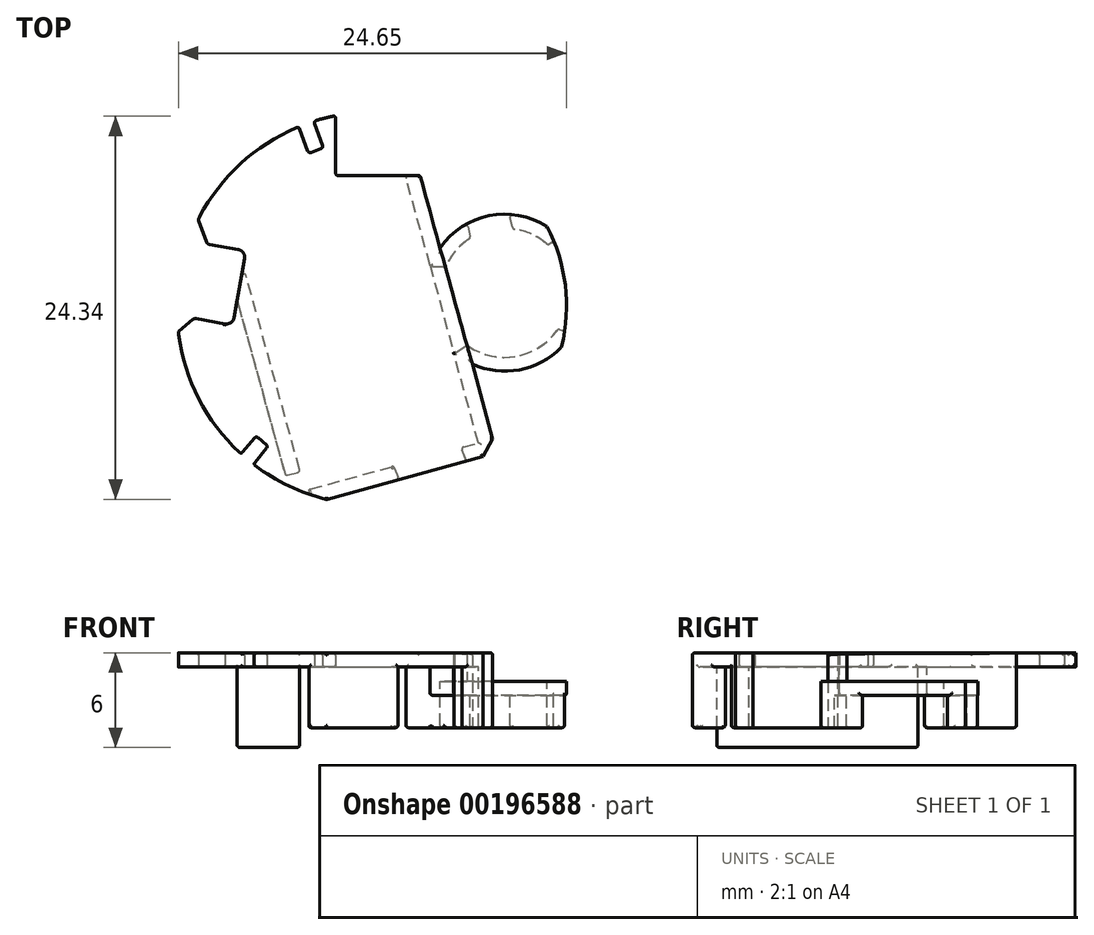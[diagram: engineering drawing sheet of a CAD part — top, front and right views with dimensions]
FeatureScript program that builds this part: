
annotation { "Feature Type Name" : "Feature", "Feature Type Description" : "" }
export const myFeature = defineFeature(function(context is Context, id is Id, definition is map)
    precondition{}
    {
        {
            var Q0;
            Q0=qCreatedBy(makeId("Top.planeOp"),FACE);
            var sketch = newSketch(context, id + "F0", { "sketchPlane" : qUnion([Q0])});
            skArc(sketch, "E0.0", {"start": v(-8.3, -9.34) * mm, "mid": v(-12.3, 2.17) * mm, "end": v(-4.6, 11.61) * mm});
            skLineSegment(sketch, "E0.1", {"start": v(-4.03, 10.06) * mm, "end": v(-4.6, 11.61) * mm});
            skLineSegment(sketch, "E0.2", {"start": v(-3.38, 10.3) * mm, "end": v(-4.03, 10.06) * mm});
            skLineSegment(sketch, "E0.3", {"start": v(-3.94, 11.85) * mm, "end": v(-3.38, 10.3) * mm});
            skArc(sketch, "E0.4", {"start": v(11.5, 4.86) * mm, "mid": v(5.15, 11.38) * mm, "end": v(-3.94, 11.85) * mm});
            skArc(sketch, "E0.5", {"start": v(9.59, 5.84) * mm, "mid": v(10.6, 5.46) * mm, "end": v(11.5, 4.86) * mm});
            skLineSegment(sketch, "E0.6", {"start": v(9.3, 7.1) * mm, "end": v(9.59, 5.84) * mm});
            skLineSegment(sketch, "E0.7", {"start": v(8.43, 6.91) * mm, "end": v(9.3, 7.1) * mm});
            skLineSegment(sketch, "E0.8", {"start": v(8.84, 5.07) * mm, "end": v(8.43, 6.91) * mm});
            skArc(sketch, "E0.9", {"start": v(11.07, 4.05) * mm, "mid": v(10.03, 4.73) * mm, "end": v(8.84, 5.07) * mm});
            skLineSegment(sketch, "E0.10", {"start": v(11.7, 4.37) * mm, "end": v(11.07, 4.05) * mm});
            skArc(sketch, "E0.11", {"start": v(12.4, -1.48) * mm, "mid": v(12.4, 1.49) * mm, "end": v(11.7, 4.37) * mm});
            skLineSegment(sketch, "E0.12", {"start": v(11.72, -1.31) * mm, "end": v(12.4, -1.48) * mm});
            skArc(sketch, "E0.13", {"start": v(5.93, -2.32) * mm, "mid": v(9.03, -3.04) * mm, "end": v(11.72, -1.31) * mm});
            skLineSegment(sketch, "E0.14", {"start": v(5.1, -2.88) * mm, "end": v(5.93, -2.32) * mm});
            skLineSegment(sketch, "E0.15", {"start": v(6.66, -8.53) * mm, "end": v(5.1, -2.88) * mm});
            skArc(sketch, "E0.16", {"start": v(12.33, -2) * mm, "mid": v(9.57, -3.82) * mm, "end": v(6.29, -3.53) * mm});
            skLineSegment(sketch, "E0.17", {"start": v(6.29, -3.53) * mm, "end": v(7.57, -8.28) * mm});
            skArc(sketch, "E0.18", {"start": v(12.33, -2) * mm, "mid": v(6.89, -10.42) * mm, "end": v(-2.99, -12.13) * mm});
            skArc(sketch, "E0.19", {"start": v(4.56, 2.62) * mm, "mid": v(5.22, 3.67) * mm, "end": v(6.15, 4.47) * mm});
            skLineSegment(sketch, "E0.20", {"start": v(4.56, 2.62) * mm, "end": v(3.62, 2.67) * mm});
            skLineSegment(sketch, "E0.21", {"start": v(3.62, 2.67) * mm, "end": v(1.3, 11.05) * mm});
            skLineSegment(sketch, "E0.22", {"start": v(5.74, 6.32) * mm, "end": v(6.15, 4.47) * mm});
            skLineSegment(sketch, "E0.23", {"start": v(4.86, 6.12) * mm, "end": v(5.74, 6.32) * mm});
            skLineSegment(sketch, "E0.24", {"start": v(5.14, 4.85) * mm, "end": v(4.86, 6.12) * mm});
            skArc(sketch, "E0.25", {"start": v(4.22, 3.85) * mm, "mid": v(4.65, 4.38) * mm, "end": v(5.14, 4.85) * mm});
            skLineSegment(sketch, "E0.26", {"start": v(2.17, 11.3) * mm, "end": v(4.22, 3.85) * mm});
            skLineSegment(sketch, "E0.27", {"start": v(1.3, 11.05) * mm, "end": v(2.17, 11.3) * mm});
            skLineSegment(sketch, "E0.28", {"start": v(5.57, -8.83) * mm, "end": v(6.66, -8.53) * mm});
            skLineSegment(sketch, "E0.29", {"start": v(5.88, -9.68) * mm, "end": v(5.57, -8.83) * mm});
            skLineSegment(sketch, "E0.30", {"start": v(7.57, -8.28) * mm, "end": v(6.94, -9.38) * mm});
            skLineSegment(sketch, "E0.31", {"start": v(6.94, -9.38) * mm, "end": v(5.88, -9.68) * mm});
            skLineSegment(sketch, "E0.32", {"start": v(1.6, -10.86) * mm, "end": v(-2.99, -12.13) * mm});
            skLineSegment(sketch, "E0.33", {"start": v(1.29, -10.01) * mm, "end": v(1.6, -10.86) * mm});
            skLineSegment(sketch, "E0.34", {"start": v(-4.14, -11.51) * mm, "end": v(1.29, -10.01) * mm});
            skLineSegment(sketch, "E0.35", {"start": v(-4.06, -11.81) * mm, "end": v(-4.14, -11.51) * mm});
            skArc(sketch, "E0.36", {"start": v(-4.06, -11.81) * mm, "mid": v(-6, -10.96) * mm, "end": v(-7.76, -9.79) * mm});
            skLineSegment(sketch, "E0.37", {"start": v(-8.3, -9.34) * mm, "end": v(-7.44, -8.32) * mm});
            skLineSegment(sketch, "E0.38", {"start": v(-7.44, -8.32) * mm, "end": v(-6.9, -8.77) * mm});
            skLineSegment(sketch, "E0.39", {"start": v(-6.9, -8.77) * mm, "end": v(-7.76, -9.79) * mm});
            skLineSegment(sketch, "E1", {"start": v(-9.35, -0.48) * mm, "end": v(-8.69, 3.26) * mm});
            skLineSegment(sketch, "E2", {"start": v(-8.69, 3.26) * mm, "end": v(-10.66, 3.61) * mm});
            skLineSegment(sketch, "E3", {"start": v(-10.66, 3.61) * mm, "end": v(-11.32, -0.13) * mm});
            skLineSegment(sketch, "E4", {"start": v(-11.32, -0.13) * mm, "end": v(-9.35, -0.48) * mm});
            skLineSegment(sketch, "E5", {"start": v(0, 0) * mm, "end": v(-7.77, 0) * mm, "construction": true});
            skLineSegment(sketch, "E6", {"start": v(3.92, 8.2) * mm, "end": v(7.03, 6.03) * mm});
            skLineSegment(sketch, "E7", {"start": v(7.03, 6.03) * mm, "end": v(8.18, 7.67) * mm});
            skLineSegment(sketch, "E8", {"start": v(8.18, 7.67) * mm, "end": v(5.06, 9.85) * mm});
            skLineSegment(sketch, "E9", {"start": v(5.06, 9.85) * mm, "end": v(3.92, 8.2) * mm});
            skLineSegment(sketch, "E10", {"start": v(0, 0) * mm, "end": v(10.4, 0) * mm, "construction": true});
            skLineSegment(sketch, "E11.0", {"start": v(-11.28, -0.65) * mm, "end": v(-9.43, -0.97) * mm});
            skLineSegment(sketch, "E12.0", {"start": v(-8.86, -0.57) * mm, "end": v(-8.2, 3.18) * mm});
            skLineSegment(sketch, "E13.0", {"start": v(-8.6, 3.76) * mm, "end": v(-10.43, 4.08) * mm});
            skLineSegment(sketch, "E14", {"start": v(-10.62, 4.24) * mm, "end": v(-11.14, 5.66) * mm});
            skLineSegment(sketch, "E15", {"start": v(-11.49, -0.7) * mm, "end": v(-12.4, -1.47) * mm});
            skArc(sketch, "E16", {"start": v(-8.2, 3.18) * mm, "mid": v(-8.28, 3.55) * mm, "end": v(-8.6, 3.76) * mm});
            skArc(sketch, "E17", {"start": v(-9.43, -0.97) * mm, "mid": v(-9.06, -0.89) * mm, "end": v(-8.86, -0.57) * mm});
            skLineSegment(sketch, "E18", {"start": v(2.17, 11.3) * mm, "end": v(1.88, 12.35) * mm});
            skLineSegment(sketch, "E19", {"start": v(7.57, -8.28) * mm, "end": v(7.95, -9.64) * mm});
            skLineSegment(sketch, "E20", {"start": v(4.56, 2.62) * mm, "end": v(5.93, -2.32) * mm});
            skLineSegment(sketch, "E21.0", {"start": v(-4.18, 10) * mm, "end": v(-4.74, 11.56) * mm});
            skLineSegment(sketch, "E22.0", {"start": v(-3.8, 11.9) * mm, "end": v(-3.24, 10.35) * mm});
            skLineSegment(sketch, "E23.0", {"start": v(-3.33, 10.16) * mm, "end": v(-3.98, 9.92) * mm});
            skArc(sketch, "E24", {"start": v(-4.18, 10) * mm, "mid": v(-4.1, 9.92) * mm, "end": v(-3.98, 9.92) * mm});
            skArc(sketch, "E25", {"start": v(-3.33, 10.16) * mm, "mid": v(-3.24, 10.24) * mm, "end": v(-3.24, 10.35) * mm});
            skLineSegment(sketch, "E26.0", {"start": v(-8.4, -9.24) * mm, "end": v(-7.55, -8.22) * mm});
            skLineSegment(sketch, "E27.0", {"start": v(-6.79, -8.86) * mm, "end": v(-7.64, -9.89) * mm});
            skLineSegment(sketch, "E28.0", {"start": v(-7.34, -8.2) * mm, "end": v(-6.8, -8.65) * mm});
            skArc(sketch, "E29", {"start": v(-6.79, -8.86) * mm, "mid": v(-6.75, -8.75) * mm, "end": v(-6.8, -8.65) * mm});
            skArc(sketch, "E30", {"start": v(-7.34, -8.2) * mm, "mid": v(-7.45, -8.17) * mm, "end": v(-7.55, -8.22) * mm});
            skLineSegment(sketch, "E31", {"start": v(6.29, -3.53) * mm, "end": v(5.93, -2.32) * mm});
            skCircle(sketch, "E32", {"center": v(0, 0) * mm, "radius": 12.49 * mm});
            skLineSegment(sketch, "E33", {"start": v(4.22, 3.85) * mm, "end": v(4.56, 2.62) * mm});
            skLineSegment(sketch, "E34", {"start": v(-4.66, -10.36) * mm, "end": v(-8.27, 2.73) * mm});
            skLineSegment(sketch, "E35", {"start": v(-8.66, 0.52) * mm, "end": v(-5.6, -10.61) * mm});
            skLineSegment(sketch, "E36", {"start": v(-5.6, -10.61) * mm, "end": v(-4.66, -10.36) * mm});
            skLineSegment(sketch, "E37", {"start": v(1.6, -10.86) * mm, "end": v(2, -12.33) * mm});
            skLineSegment(sketch, "E38", {"start": v(5.88, -9.68) * mm, "end": v(6.2, -10.84) * mm});
            skLineSegment(sketch, "E39", {"start": v(6.2, -10.84) * mm, "end": v(5.88, -9.68) * mm});
            skLineSegment(sketch, "E40", {"start": v(5.88, -9.68) * mm, "end": v(1.6, -10.86) * mm});
            skPoint(sketch, "E41.visualSharp", {"position": v(-10.57, 4.1) * mm});
            skArc(sketch, "E41.filletArc", {"start": v(-10.62, 4.24) * mm, "mid": v(-10.55, 4.13) * mm, "end": v(-10.43, 4.08) * mm});
            skPoint(sketch, "E42.visualSharp", {"position": v(-11.4, -0.63) * mm});
            skArc(sketch, "E42.filletArc", {"start": v(-11.28, -0.65) * mm, "mid": v(-11.4, -0.65) * mm, "end": v(-11.49, -0.7) * mm});
            skLineSegment(sketch, "E43.bottom", {"start": v(-2.4, 13.27) * mm, "end": v(2.4, 13.27) * mm});
            skLineSegment(sketch, "E43.top", {"start": v(-2.4, 8.45) * mm, "end": v(2.4, 8.45) * mm});
            skLineSegment(sketch, "E43.left", {"start": v(-2.4, 13.27) * mm, "end": v(-2.4, 8.45) * mm});
            skLineSegment(sketch, "E43.right", {"start": v(2.4, 13.27) * mm, "end": v(2.4, 8.45) * mm});
            skLineSegment(sketch, "E44", {"start": v(2.4, 8.45) * mm, "end": v(2.95, 8.45) * mm});
            skCircle(sketch, "E45", {"center": v(8.33, 1) * mm, "radius": 4.1 * mm});
            skCircle(sketch, "E46", {"center": v(8.33, 1) * mm, "radius": 5 * mm});
            skArc(sketch, "E47", {"start": v(11.94, -2.46) * mm, "mid": v(12.18, 1.46) * mm, "end": v(11.02, 5.22) * mm});
            skLineSegment(sketch, "E48", {"start": v(3.62, 2.67) * mm, "end": v(5.1, -2.88) * mm});
            skSolve(sketch);
        }
        {
            var Q0;
            {var subQ30=sQuery(id+"F0.wireOp",EDGE,"E0.28");Q0=makeQuery(id+"F0.imprint","IMPRINT",FACE,{"disambiguationData":[TD([[makeQuery(id+"F0.imprint","IMPRINT",EDGE,{"derivedFrom":subQ30}),1.0]])]});}
            var Q1;
            {var subQ0=sQuery(id+"F0.wireOp",EDGE,"E34");Q1=makeQuery(id+"F0.imprint","IMPRINT",FACE,{"disambiguationData":[TD([[makeQuery(id+"F0.imprint","IMPRINT",EDGE,{"derivedFrom":subQ0}),1.0]])]});}
            var Q2;
            {var subQ1=sQuery(id+"F0.wireOp",EDGE,"E0.32");Q2=makeQuery(id+"F0.imprint","IMPRINT",FACE,{"disambiguationData":[TD([[makeQuery(id+"F0.imprint","IMPRINT",EDGE,{"derivedFrom":subQ1}),-1.0]])]});}
            var Q3;
            {var subQ0=sQuery(id+"F0.wireOp",EDGE,"E44");Q3=makeQuery(id+"F0.imprint","IMPRINT",FACE,{"disambiguationData":[TD([[makeQuery(id+"F0.imprint","IMPRINT",EDGE,{"derivedFrom":subQ0}),-1.0]])]});}
            var Q4;
            {var subQ6=sQuery(id+"F0.wireOp",EDGE,"E0.20");Q4=makeQuery(id+"F0.imprint","IMPRINT",FACE,{"disambiguationData":[TD([[makeQuery(id+"F0.imprint","IMPRINT",EDGE,{"derivedFrom":subQ6}),1.0]])]});}
            var Q5;
            {var subQ0=sQuery(id+"F0.wireOp",EDGE,"E31");Q5=makeQuery(id+"F0.imprint","IMPRINT",FACE,{"disambiguationData":[TD([[makeQuery(id+"F0.imprint","IMPRINT",EDGE,{"derivedFrom":subQ0}),1.0]])]});}
            var Q6;
            {var subQ4=sQuery(id+"F0.wireOp",EDGE,"E0.15");Q6=makeQuery(id+"F0.imprint","IMPRINT",FACE,{"disambiguationData":[TD([[makeQuery(id+"F0.imprint","IMPRINT",EDGE,{"derivedFrom":subQ4}),-1.0]])]});}
            var Q7;
            {var subQ0=sQuery(id+"F0.wireOp",EDGE,"E0.20");Q7=makeQuery(id+"F0.imprint","IMPRINT",FACE,{"disambiguationData":[TD([[makeQuery(id+"F0.imprint","IMPRINT",EDGE,{"derivedFrom":subQ0}),-1.0]])]});}
            var Q8;
            {var subQ0=sQuery(id+"F0.wireOp",EDGE,"E20");Q8=makeQuery(id+"F0.imprint","IMPRINT",FACE,{"disambiguationData":[TD([[makeQuery(id+"F0.imprint","IMPRINT",EDGE,{"derivedFrom":subQ0}),-1.0]])]});}
            var Q9;
            {var subQ0=sQuery(id+"F0.wireOp",EDGE,"E48");var subQ1=sQuery(id+"F0.wireOp",EDGE,"E46");var subQ3=makeQuery(id+"F0.imprint","INTERSECT",VERTEX,{"derivedFrom":[subQ1,subQ0]});Q9=makeQuery(id+"F0.imprint","IMPRINT",FACE,{"disambiguationData":[TD([[makeQuery(id+"F0.imprint","IMPRINT",EDGE,{"disambiguationData":[TD([[subQ3,1.0]])],"derivedFrom":subQ1}),1.0]])]});}
            extrude(context, id + "F1", {"entities" : qUnion([Q0, Q1, Q2, Q3, Q4, Q5, Q6, Q7, Q8, Q9]), "depth" : .9 * mm});
        }
        {
            var Q0;
            {var subQ1=sQuery(id+"F0.wireOp",EDGE,"E0.32");Q0=makeQuery(id+"F0.imprint","IMPRINT",FACE,{"disambiguationData":[TD([[makeQuery(id+"F0.imprint","IMPRINT",EDGE,{"derivedFrom":subQ1}),-1.0]])]});}
            var Q1;
            {var subQ9=sQuery(id+"F0.wireOp",EDGE,"E0.17");Q1=makeQuery(id+"F0.imprint","IMPRINT",FACE,{"disambiguationData":[TD([[makeQuery(id+"F0.imprint","IMPRINT",EDGE,{"derivedFrom":subQ9}),-1.0]])]});}
            var Q2;
            {var subQ3=sQuery(id+"F0.wireOp",EDGE,"E44");Q2=makeQuery(id+"F0.imprint","IMPRINT",FACE,{"disambiguationData":[TD([[makeQuery(id+"F0.imprint","IMPRINT",EDGE,{"derivedFrom":subQ3}),-1.0]])]});}
            var Q3;
            {var subQ0=sQuery(id+"F0.wireOp",EDGE,"E0.20");Q3=makeQuery(id+"F0.imprint","IMPRINT",FACE,{"disambiguationData":[TD([[makeQuery(id+"F0.imprint","IMPRINT",EDGE,{"derivedFrom":subQ0}),-1.0]])]});}
            var Q4;
            {var subQ4=sQuery(id+"F0.wireOp",EDGE,"E0.15");Q4=makeQuery(id+"F0.imprint","IMPRINT",FACE,{"disambiguationData":[TD([[makeQuery(id+"F0.imprint","IMPRINT",EDGE,{"derivedFrom":subQ4}),-1.0]])]});}
            extrude(context, id + "F2", {"entities" : qUnion([Q0, Q1, Q2, Q3, Q4]), "operationType" : NewBodyOperationType.ADD, "oppositeDirection" : true, "depth" : (5.2 - .1 - 1.25) * mm});
        }
        {
            var Q0;
            {var subQ0=sQuery(id+"F0.wireOp",EDGE,"E34");Q0=makeQuery(id+"F0.imprint","IMPRINT",FACE,{"disambiguationData":[TD([[makeQuery(id+"F0.imprint","IMPRINT",EDGE,{"derivedFrom":subQ0}),1.0]])]});}
            extrude(context, id + "F3", {"entities" : qUnion([Q0]), "operationType" : NewBodyOperationType.ADD, "oppositeDirection" : true, "depth" : (5.2 - .1) * mm});
        }
        {
            var Q0;
            {var subQ3=sQuery(id+"F0.wireOp",EDGE,"E31");Q0=makeQuery(id+"F0.imprint","IMPRINT",FACE,{"disambiguationData":[TD([[makeQuery(id+"F0.imprint","IMPRINT",EDGE,{"derivedFrom":subQ3}),-1.0]])]});}
            var Q1;
            {var subQ3=sQuery(id+"F0.wireOp",EDGE,"E20");Q1=makeQuery(id+"F0.imprint","IMPRINT",FACE,{"disambiguationData":[TD([[makeQuery(id+"F0.imprint","IMPRINT",EDGE,{"derivedFrom":subQ3}),1.0]])]});}
            var Q2;
            {var subQ5=sQuery(id+"F0.wireOp",EDGE,"E33");Q2=makeQuery(id+"F0.imprint","IMPRINT",FACE,{"disambiguationData":[TD([[makeQuery(id+"F0.imprint","IMPRINT",EDGE,{"derivedFrom":subQ5}),1.0]])]});}
            var Q3;
            {var subQ0=sQuery(id+"F0.wireOp",EDGE,"E45");var subQ1=sQuery(id+"F0.wireOp",EDGE,"E0.8");var subQ2=makeQuery(id+"F0.imprint","INTERSECT",VERTEX,{"derivedFrom":[subQ1,subQ0]});Q3=makeQuery(id+"F0.imprint","IMPRINT",FACE,{"disambiguationData":[TD([[makeQuery(id+"F0.imprint","IMPRINT",EDGE,{"disambiguationData":[TD([[subQ2,-1.0]])],"derivedFrom":subQ1}),1.0]])]});}
            var Q4;
            {var subQ4=sQuery(id+"F0.wireOp",EDGE,"E45");var subQ5=sQuery(id+"F0.wireOp",EDGE,"E0.8");var subQ6=makeQuery(id+"F0.imprint","INTERSECT",VERTEX,{"derivedFrom":[subQ5,subQ4]});Q4=makeQuery(id+"F0.imprint","IMPRINT",FACE,{"disambiguationData":[TD([[makeQuery(id+"F0.imprint","IMPRINT",EDGE,{"disambiguationData":[TD([[subQ6,-1.0]])],"derivedFrom":subQ5}),-1.0]])]});}
            var Q5;
            {var subQ0=sQuery(id+"F0.wireOp",EDGE,"E45");var subQ1=sQuery(id+"F0.wireOp",EDGE,"E0.10");var subQ2=makeQuery(id+"F0.imprint","INTERSECT",VERTEX,{"derivedFrom":[subQ1,subQ0]});Q5=makeQuery(id+"F0.imprint","IMPRINT",FACE,{"disambiguationData":[TD([[makeQuery(id+"F0.imprint","IMPRINT",EDGE,{"disambiguationData":[TD([[subQ2,1.0]])],"derivedFrom":subQ1}),1.0]])]});}
            var Q6;
            {var subQ0=sQuery(id+"F0.wireOp",EDGE,"E45");var subQ1=sQuery(id+"F0.wireOp",EDGE,"E0.12");var subQ2=makeQuery(id+"F0.imprint","INTERSECT",VERTEX,{"derivedFrom":[subQ1,subQ0]});Q6=makeQuery(id+"F0.imprint","IMPRINT",FACE,{"disambiguationData":[TD([[makeQuery(id+"F0.imprint","IMPRINT",EDGE,{"disambiguationData":[TD([[subQ2,-1.0]])],"derivedFrom":subQ1}),1.0]])]});}
            var Q7;
            {var subQ0=sQuery(id+"F0.wireOp",EDGE,"E20");Q7=makeQuery(id+"F0.imprint","IMPRINT",FACE,{"disambiguationData":[TD([[makeQuery(id+"F0.imprint","IMPRINT",EDGE,{"derivedFrom":subQ0}),-1.0]])]});}
            var Q8;
            {var subQ0=sQuery(id+"F0.wireOp",EDGE,"E0.20");Q8=makeQuery(id+"F0.imprint","IMPRINT",FACE,{"disambiguationData":[TD([[makeQuery(id+"F0.imprint","IMPRINT",EDGE,{"derivedFrom":subQ0}),-1.0]])]});}
            var Q9;
            {var subQ0=sQuery(id+"F0.wireOp",EDGE,"E31");Q9=makeQuery(id+"F0.imprint","IMPRINT",FACE,{"disambiguationData":[TD([[makeQuery(id+"F0.imprint","IMPRINT",EDGE,{"derivedFrom":subQ0}),1.0]])]});}
            var Q10;
            {var subQ4=sQuery(id+"F0.wireOp",EDGE,"E0.20");Q10=makeQuery(id+"F0.imprint","IMPRINT",FACE,{"disambiguationData":[TD([[makeQuery(id+"F0.imprint","IMPRINT",EDGE,{"derivedFrom":subQ4}),1.0]])]});}
            extrude(context, id + "F4", {"entities" : qUnion([Q0, Q1, Q2, Q3, Q4, Q5, Q6, Q7, Q8, Q9, Q10]), "operationType" : NewBodyOperationType.ADD, "oppositeDirection" : true, "depth" : 1.8 * mm});
        }
        {
            var Q0;
            {var subQ5=sQuery(id+"F0.wireOp",EDGE,"E33");Q0=makeQuery(id+"F0.imprint","IMPRINT",FACE,{"disambiguationData":[TD([[makeQuery(id+"F0.imprint","IMPRINT",EDGE,{"derivedFrom":subQ5}),1.0]])]});}
            var Q1;
            {var subQ4=sQuery(id+"F0.wireOp",EDGE,"E45");var subQ5=sQuery(id+"F0.wireOp",EDGE,"E0.8");var subQ6=makeQuery(id+"F0.imprint","INTERSECT",VERTEX,{"derivedFrom":[subQ5,subQ4]});Q1=makeQuery(id+"F0.imprint","IMPRINT",FACE,{"disambiguationData":[TD([[makeQuery(id+"F0.imprint","IMPRINT",EDGE,{"disambiguationData":[TD([[subQ6,-1.0]])],"derivedFrom":subQ5}),-1.0]])]});}
            var Q2;
            {var subQ3=sQuery(id+"F0.wireOp",EDGE,"E31");Q2=makeQuery(id+"F0.imprint","IMPRINT",FACE,{"disambiguationData":[TD([[makeQuery(id+"F0.imprint","IMPRINT",EDGE,{"derivedFrom":subQ3}),-1.0]])]});}
            extrude(context, id + "F5", {"entities" : qUnion([Q0, Q1, Q2]), "operationType" : NewBodyOperationType.ADD, "oppositeDirection" : true, "depth" : 3.85 * mm});
        }
        {
            var Q0;
            {var subQ5=sQuery(id+"F0.wireOp",EDGE,"E33");Q0=makeQuery(id+"F0.imprint","IMPRINT",FACE,{"disambiguationData":[TD([[makeQuery(id+"F0.imprint","IMPRINT",EDGE,{"derivedFrom":subQ5}),1.0]])]});}
            var Q1;
            {var subQ0=sQuery(id+"F0.wireOp",EDGE,"E45");var subQ1=sQuery(id+"F0.wireOp",EDGE,"E0.8");var subQ2=makeQuery(id+"F0.imprint","INTERSECT",VERTEX,{"derivedFrom":[subQ1,subQ0]});Q1=makeQuery(id+"F0.imprint","IMPRINT",FACE,{"disambiguationData":[TD([[makeQuery(id+"F0.imprint","IMPRINT",EDGE,{"disambiguationData":[TD([[subQ2,-1.0]])],"derivedFrom":subQ1}),1.0]])]});}
            var Q2;
            {var subQ4=sQuery(id+"F0.wireOp",EDGE,"E45");var subQ5=sQuery(id+"F0.wireOp",EDGE,"E0.8");var subQ6=makeQuery(id+"F0.imprint","INTERSECT",VERTEX,{"derivedFrom":[subQ5,subQ4]});Q2=makeQuery(id+"F0.imprint","IMPRINT",FACE,{"disambiguationData":[TD([[makeQuery(id+"F0.imprint","IMPRINT",EDGE,{"disambiguationData":[TD([[subQ6,-1.0]])],"derivedFrom":subQ5}),-1.0]])]});}
            var Q3;
            {var subQ0=sQuery(id+"F0.wireOp",EDGE,"E45");var subQ1=sQuery(id+"F0.wireOp",EDGE,"E0.10");var subQ2=makeQuery(id+"F0.imprint","INTERSECT",VERTEX,{"derivedFrom":[subQ1,subQ0]});Q3=makeQuery(id+"F0.imprint","IMPRINT",FACE,{"disambiguationData":[TD([[makeQuery(id+"F0.imprint","IMPRINT",EDGE,{"disambiguationData":[TD([[subQ2,1.0]])],"derivedFrom":subQ1}),1.0]])]});}
            var Q4;
            {var subQ3=sQuery(id+"F0.wireOp",EDGE,"E20");Q4=makeQuery(id+"F0.imprint","IMPRINT",FACE,{"disambiguationData":[TD([[makeQuery(id+"F0.imprint","IMPRINT",EDGE,{"derivedFrom":subQ3}),1.0]])]});}
            var Q5;
            {var subQ3=sQuery(id+"F0.wireOp",EDGE,"E31");Q5=makeQuery(id+"F0.imprint","IMPRINT",FACE,{"disambiguationData":[TD([[makeQuery(id+"F0.imprint","IMPRINT",EDGE,{"derivedFrom":subQ3}),-1.0]])]});}
            var Q6;
            {var subQ0=sQuery(id+"F0.wireOp",EDGE,"E45");var subQ1=sQuery(id+"F0.wireOp",EDGE,"E0.12");var subQ2=makeQuery(id+"F0.imprint","INTERSECT",VERTEX,{"derivedFrom":[subQ1,subQ0]});Q6=makeQuery(id+"F0.imprint","IMPRINT",FACE,{"disambiguationData":[TD([[makeQuery(id+"F0.imprint","IMPRINT",EDGE,{"disambiguationData":[TD([[subQ2,-1.0]])],"derivedFrom":subQ1}),1.0]])]});}
            extrude(context, id + "F6", {"entities" : qUnion([Q0, Q1, Q2, Q3, Q4, Q5, Q6]), "operationType" : NewBodyOperationType.REMOVE, "oppositeDirection" : true, "depth" : .9 * mm});
        }
        {
            var Q0;
            Q0=makeQuery(id+"F1.opExtrude","CAP_EDGE",EDGE,{"disambiguationData":[OSD([sQuery(id+"F0.wireOp",EDGE,"E0.31"),sQuery(id+"F0.wireOp",EDGE,"E0.32"),sQuery(id+"F0.wireOp",EDGE,"E40")])],"isStart":false});
            var Q1;
            {var subQ0=sQuery(id+"F0.wireOp",EDGE,"E32");var subQ1=makeQuery(id+"F0.imprint","INTERSECT",VERTEX,{"derivedFrom":[sQuery(id+"F0.wireOp",EDGE,"E0.35"),subQ0]});Q1=makeQuery(id+"F1.opExtrude","CAP_EDGE",EDGE,{"disambiguationData":[OSD([subQ0]),TDD([makeQuery(id+"F0.imprint","IMPRINT",EDGE,{"disambiguationData":[TD([[subQ1,1.0]])],"derivedFrom":subQ0}),makeQuery(id+"F0.imprint","IMPRINT",EDGE,{"disambiguationData":[TD([[makeQuery(id+"F0.imprint","INTERSECT",VERTEX,{"derivedFrom":[sQuery(id+"F0.wireOp",EDGE,"E0.32"),subQ0]}),1.0]])],"derivedFrom":subQ0})])],"isStart":false});}
            var Q2;
            Q2=makeQuery(id+"F1.opExtrude","CAP_EDGE",EDGE,{"disambiguationData":[OSD([sQuery(id+"F0.wireOp",EDGE,"E0.30")])],"isStart":false});
            var Q3;
            Q3=makeQuery(id+"F1.opExtrude","CAP_EDGE",EDGE,{"disambiguationData":[OSD([sQuery(id+"F0.wireOp",EDGE,"E0.17")])],"isStart":false});
            var Q4;
            Q4=makeQuery(id+"F1.opExtrude","CAP_EDGE",EDGE,{"disambiguationData":[OSD([sQuery(id+"F0.wireOp",EDGE,"E43.top"),sQuery(id+"F0.wireOp",EDGE,"E44")])],"isStart":false});
            var Q5;
            Q5=makeQuery(id+"F1.opExtrude","CAP_EDGE",EDGE,{"disambiguationData":[OSD([sQuery(id+"F0.wireOp",EDGE,"E43.left")])],"isStart":false});
            var Q6;
            {var subQ0=sQuery(id+"F0.wireOp",EDGE,"E32");Q6=makeQuery(id+"F1.opExtrude","CAP_EDGE",EDGE,{"disambiguationData":[OSD([subQ0]),TDD([makeQuery(id+"F0.imprint","IMPRINT",EDGE,{"disambiguationData":[TD([[makeQuery(id+"F0.imprint","INTERSECT",VERTEX,{"derivedFrom":[sQuery(id+"F0.wireOp",EDGE,"E22.0"),subQ0]}),1.0]])],"derivedFrom":subQ0})])],"isStart":false});}
            var Q7;
            Q7=makeQuery(id+"F1.opExtrude","CAP_EDGE",EDGE,{"disambiguationData":[OSD([sQuery(id+"F0.wireOp",EDGE,"E23.0")])],"isStart":false});
            var Q8;
            {var subQ0=sQuery(id+"F0.wireOp",EDGE,"E32");Q8=makeQuery(id+"F1.opExtrude","CAP_EDGE",EDGE,{"disambiguationData":[OSD([subQ0]),TDD([makeQuery(id+"F0.imprint","IMPRINT",EDGE,{"disambiguationData":[TD([[makeQuery(id+"F0.imprint","INTERSECT",VERTEX,{"derivedFrom":[sQuery(id+"F0.wireOp",EDGE,"E14"),subQ0]}),1.0]])],"derivedFrom":subQ0})])],"isStart":false});}
            var Q9;
            Q9=makeQuery(id+"F1.opExtrude","CAP_EDGE",EDGE,{"disambiguationData":[OSD([sQuery(id+"F0.wireOp",EDGE,"E14")])],"isStart":false});
            var Q10;
            Q10=makeQuery(id+"F1.opExtrude","CAP_EDGE",EDGE,{"disambiguationData":[OSD([sQuery(id+"F0.wireOp",EDGE,"E28.0")])],"isStart":false});
            var Q11;
            {var subQ0=sQuery(id+"F0.wireOp",EDGE,"E32");Q11=makeQuery(id+"F1.opExtrude","CAP_EDGE",EDGE,{"disambiguationData":[OSD([subQ0]),TDD([makeQuery(id+"F0.imprint","IMPRINT",EDGE,{"disambiguationData":[TD([[makeQuery(id+"F0.imprint","INTERSECT",VERTEX,{"derivedFrom":[sQuery(id+"F0.wireOp",EDGE,"E15"),subQ0]}),-1.0]])],"derivedFrom":subQ0})])],"isStart":false});}
            var Q12;
            Q12=makeQuery(id+"F1.opExtrude","CAP_EDGE",EDGE,{"disambiguationData":[OSD([sQuery(id+"F0.wireOp",EDGE,"E15")])],"isStart":false});
            var Q13;
            Q13=makeQuery(id+"F6.boolean.opBoolean","COPY",EDGE,{"derivedFrom":makeQuery(id+"F6.opExtrude","CAP_EDGE",EDGE,{"disambiguationData":[OSD([sQuery(id+"F0.wireOp",EDGE,"E46")])],"isStart":false})});
            var Q14;
            Q14=makeQuery(id+"F6.boolean.opBoolean","COPY",EDGE,{"derivedFrom":makeQuery(id+"F6.opExtrude","CAP_EDGE",EDGE,{"disambiguationData":[OSD([sQuery(id+"F0.wireOp",EDGE,"E47")])],"isStart":false})});
            var Q15;
            Q15=makeQuery(id+"F6.boolean.opBoolean","COPY",EDGE,{"derivedFrom":makeQuery(id+"F6.opExtrude","CAP_EDGE",EDGE,{"disambiguationData":[OSD([sQuery(id+"F0.wireOp",EDGE,"E0.16")])],"isStart":false})});
            var Q16;
            Q16=makeQuery(id+"F4.opExtrude","CAP_EDGE",EDGE,{"disambiguationData":[OSD([sQuery(id+"F0.wireOp",EDGE,"E47")])],"isStart":false});
            var Q17;
            Q17=makeQuery(id+"F5.opExtrude","SWEPT_EDGE",EDGE,{"disambiguationData":[OSD([sQuery(id+"F0.wireOp",EDGE,"E0.10"),sQuery(id+"F0.wireOp",EDGE,"E47")])]});
            var Q18;
            Q18=makeQuery(id+"F5.opExtrude","SWEPT_EDGE",EDGE,{"disambiguationData":[OSD([sQuery(id+"F0.wireOp",EDGE,"E0.10"),sQuery(id+"F0.wireOp",EDGE,"E45")])]});
            var Q19;
            Q19=makeQuery(id+"F5.opExtrude","SWEPT_EDGE",EDGE,{"disambiguationData":[OSD([sQuery(id+"F0.wireOp",EDGE,"E0.8"),sQuery(id+"F0.wireOp",EDGE,"E45")])]});
            var Q20;
            {var subQ0=sQuery(id+"F0.wireOp",EDGE,"E45");Q20=makeQuery(id+"F5.opExtrude","CAP_EDGE",EDGE,{"disambiguationData":[OSD([subQ0]),TDD([makeQuery(id+"F0.imprint","IMPRINT",EDGE,{"disambiguationData":[TD([[makeQuery(id+"F0.imprint","INTERSECT",VERTEX,{"derivedFrom":[sQuery(id+"F0.wireOp",EDGE,"E0.8"),subQ0]}),1.0]])],"derivedFrom":subQ0})])],"isStart":false});}
            var Q21;
            Q21=makeQuery(id+"F5.opExtrude","CAP_EDGE",EDGE,{"disambiguationData":[OSD([sQuery(id+"F0.wireOp",EDGE,"E0.10")])],"isStart":false});
            var Q22;
            {var subQ0=sQuery(id+"F0.wireOp",EDGE,"E47");Q22=makeQuery(id+"F5.opExtrude","CAP_EDGE",EDGE,{"disambiguationData":[OSD([subQ0]),TDD([makeQuery(id+"F0.imprint","IMPRINT",EDGE,{"disambiguationData":[TD([[makeQuery(id+"F0.imprint","INTERSECT",VERTEX,{"derivedFrom":[sQuery(id+"F0.wireOp",EDGE,"E46"),subQ0]}),1.0]])],"derivedFrom":subQ0})])],"isStart":false});}
            var Q23;
            {var subQ0=sQuery(id+"F0.wireOp",EDGE,"E46");var subQ1=makeQuery(id+"F0.imprint","INTERSECT",VERTEX,{"derivedFrom":[sQuery(id+"F0.wireOp",EDGE,"E0.6"),subQ0]});Q23=makeQuery(id+"F5.opExtrude","CAP_EDGE",EDGE,{"disambiguationData":[OSD([subQ0]),TDD([makeQuery(id+"F0.imprint","IMPRINT",EDGE,{"disambiguationData":[TD([[subQ1,1.0]])],"derivedFrom":subQ0}),makeQuery(id+"F0.imprint","IMPRINT",EDGE,{"disambiguationData":[TD([[subQ1,-1.0]])],"derivedFrom":subQ0})])],"isStart":false});}
            var Q24;
            Q24=makeQuery(id+"F5.opExtrude","CAP_EDGE",EDGE,{"disambiguationData":[OSD([sQuery(id+"F0.wireOp",EDGE,"E0.8")])],"isStart":false});
            var Q25;
            Q25=makeQuery(id+"F5.opExtrude","SWEPT_EDGE",EDGE,{"disambiguationData":[OSD([sQuery(id+"F0.wireOp",EDGE,"E0.22"),sQuery(id+"F0.wireOp",EDGE,"E45")])]});
            var Q26;
            {var subQ0=sQuery(id+"F0.wireOp",EDGE,"E45");Q26=makeQuery(id+"F5.opExtrude","CAP_EDGE",EDGE,{"disambiguationData":[OSD([subQ0]),TDD([makeQuery(id+"F0.imprint","IMPRINT",EDGE,{"disambiguationData":[TD([[makeQuery(id+"F0.imprint","INTERSECT",VERTEX,{"derivedFrom":[sQuery(id+"F0.wireOp",EDGE,"E0.22"),subQ0]}),-1.0]])],"derivedFrom":subQ0})])],"isStart":false});}
            var Q27;
            {var subQ0=sQuery(id+"F0.wireOp",EDGE,"E47");var subQ1=sQuery(id+"F0.wireOp",EDGE,"E0.16");Q27=makeQuery(id+"F5.boolean.opBoolean","MERGE",EDGE,{"derivedFrom":[makeQuery(id+"F4.opExtrude","SWEPT_EDGE",EDGE,{"disambiguationData":[OSD([subQ1,subQ0])]}),makeQuery(id+"F5.opExtrude","SWEPT_EDGE",EDGE,{"disambiguationData":[OSD([subQ1,subQ0])]})]});}
            var Q28;
            Q28=makeQuery(id+"F5.opExtrude","SWEPT_EDGE",EDGE,{"disambiguationData":[OSD([sQuery(id+"F0.wireOp",EDGE,"E0.12"),sQuery(id+"F0.wireOp",EDGE,"E47")])]});
            var Q29;
            Q29=makeQuery(id+"F5.opExtrude","SWEPT_EDGE",EDGE,{"disambiguationData":[OSD([sQuery(id+"F0.wireOp",EDGE,"E0.12"),sQuery(id+"F0.wireOp",EDGE,"E45")])]});
            var Q30;
            Q30=makeQuery(id+"F5.opExtrude","CAP_EDGE",EDGE,{"disambiguationData":[OSD([sQuery(id+"F0.wireOp",EDGE,"E0.12")])],"isStart":false});
            var Q31;
            Q31=makeQuery(id+"F5.opExtrude","CAP_EDGE",EDGE,{"disambiguationData":[OSD([sQuery(id+"F0.wireOp",EDGE,"E0.16")])],"isStart":false});
            var Q32;
            {var subQ0=sQuery(id+"F0.wireOp",EDGE,"E47");Q32=makeQuery(id+"F5.opExtrude","CAP_EDGE",EDGE,{"disambiguationData":[OSD([subQ0]),TDD([makeQuery(id+"F0.imprint","IMPRINT",EDGE,{"disambiguationData":[TD([[makeQuery(id+"F0.imprint","INTERSECT",VERTEX,{"derivedFrom":[sQuery(id+"F0.wireOp",EDGE,"E0.16"),subQ0]}),-1.0]])],"derivedFrom":subQ0})])],"isStart":false});}
            var Q33;
            {var subQ0=sQuery(id+"F0.wireOp",EDGE,"E45");Q33=makeQuery(id+"F5.opExtrude","CAP_EDGE",EDGE,{"disambiguationData":[OSD([subQ0]),TDD([makeQuery(id+"F0.imprint","IMPRINT",EDGE,{"disambiguationData":[TD([[makeQuery(id+"F0.imprint","INTERSECT",VERTEX,{"derivedFrom":[sQuery(id+"F0.wireOp",EDGE,"E0.12"),subQ0]}),1.0]])],"derivedFrom":subQ0})])],"isStart":false});}
            var Q34;
            Q34=makeQuery(id+"F5.opExtrude","CAP_EDGE",EDGE,{"disambiguationData":[OSD([sQuery(id+"F0.wireOp",EDGE,"E0.22")])],"isStart":false});
            var Q35;
            {var subQ0=sQuery(id+"F0.wireOp",EDGE,"E46");var subQ1=makeQuery(id+"F0.imprint","INTERSECT",VERTEX,{"derivedFrom":[sQuery(id+"F0.wireOp",EDGE,"E0.24"),subQ0]});Q35=makeQuery(id+"F5.opExtrude","CAP_EDGE",EDGE,{"disambiguationData":[OSD([subQ0]),TDD([makeQuery(id+"F0.imprint","IMPRINT",EDGE,{"disambiguationData":[TD([[subQ1,1.0]])],"derivedFrom":subQ0}),makeQuery(id+"F0.imprint","IMPRINT",EDGE,{"disambiguationData":[TD([[subQ1,-1.0]])],"derivedFrom":subQ0})])],"isStart":false});}
            var Q36;
            Q36=makeQuery(id+"F2.opExtrude","CAP_EDGE",EDGE,{"disambiguationData":[OSD([sQuery(id+"F0.wireOp",EDGE,"E0.26"),sQuery(id+"F0.wireOp",EDGE,"E33")])],"isStart":false});
            var Q37;
            Q37=makeQuery(id+"F5.opExtrude","SWEPT_EDGE",EDGE,{"disambiguationData":[OSD([sQuery(id+"F0.wireOp",EDGE,"E0.22"),sQuery(id+"F0.wireOp",EDGE,"E46")])]});
            var Q38;
            Q38=makeQuery(id+"F5.opExtrude","SWEPT_EDGE",EDGE,{"disambiguationData":[OSD([sQuery(id+"F0.wireOp",EDGE,"E0.8"),sQuery(id+"F0.wireOp",EDGE,"E46")])]});
            var Q39;
            Q39=makeQuery(id+"F2.opExtrude","CAP_EDGE",EDGE,{"disambiguationData":[OSD([sQuery(id+"F0.wireOp",EDGE,"E0.20")])],"isStart":false});
            var Q40;
            Q40=makeQuery(id+"F2.opExtrude","CAP_EDGE",EDGE,{"disambiguationData":[OSD([sQuery(id+"F0.wireOp",EDGE,"E0.21")])],"isStart":false});
            var Q41;
            Q41=makeQuery(id+"F2.opExtrude","CAP_EDGE",EDGE,{"disambiguationData":[OSD([sQuery(id+"F0.wireOp",EDGE,"E43.top"),sQuery(id+"F0.wireOp",EDGE,"E44")])],"isStart":false});
            var Q42;
            Q42=makeQuery(id+"F2.opExtrude","SWEPT_EDGE",EDGE,{"disambiguationData":[OSD([sQuery(id+"F0.wireOp",EDGE,"E0.21"),sQuery(id+"F0.wireOp",EDGE,"E43.top")])]});
            var Q43;
            {var subQ0=sQuery(id+"F0.wireOp",EDGE,"E44");var subQ1=sQuery(id+"F0.wireOp",EDGE,"E0.26");Q43=makeQuery(id+"F2.boolean.opBoolean","MERGE",EDGE,{"derivedFrom":[makeQuery(id+"F1.opExtrude","SWEPT_EDGE",EDGE,{"disambiguationData":[OSD([subQ1,subQ0])]}),makeQuery(id+"F2.opExtrude","SWEPT_EDGE",EDGE,{"disambiguationData":[OSD([subQ1,subQ0])]})]});}
            var Q44;
            Q44=makeQuery(id+"F1.opExtrude","CAP_EDGE",EDGE,{"disambiguationData":[OSD([sQuery(id+"F0.wireOp",EDGE,"E43.top"),sQuery(id+"F0.wireOp",EDGE,"E44")])],"isStart":true});
            var Q45;
            Q45=makeQuery(id+"F1.opExtrude","CAP_EDGE",EDGE,{"disambiguationData":[OSD([sQuery(id+"F0.wireOp",EDGE,"E43.left")])],"isStart":true});
            var Q46;
            {var subQ0=sQuery(id+"F0.wireOp",EDGE,"E32");Q46=makeQuery(id+"F1.opExtrude","CAP_EDGE",EDGE,{"disambiguationData":[OSD([subQ0]),TDD([makeQuery(id+"F0.imprint","IMPRINT",EDGE,{"disambiguationData":[TD([[makeQuery(id+"F0.imprint","INTERSECT",VERTEX,{"derivedFrom":[sQuery(id+"F0.wireOp",EDGE,"E22.0"),subQ0]}),1.0]])],"derivedFrom":subQ0})])],"isStart":true});}
            var Q47;
            Q47=makeQuery(id+"F1.opExtrude","SWEPT_EDGE",EDGE,{"disambiguationData":[OSD([sQuery(id+"F0.wireOp",EDGE,"E32"),sQuery(id+"F0.wireOp",EDGE,"E43.left")])]});
            var Q48;
            Q48=makeQuery(id+"F1.opExtrude","CAP_EDGE",EDGE,{"disambiguationData":[OSD([sQuery(id+"F0.wireOp",EDGE,"E23.0")])],"isStart":true});
            var Q49;
            Q49=makeQuery(id+"F1.opExtrude","SWEPT_EDGE",EDGE,{"disambiguationData":[OSD([sQuery(id+"F0.wireOp",EDGE,"E21.0"),sQuery(id+"F0.wireOp",EDGE,"E32")])]});
            var Q50;
            Q50=makeQuery(id+"F1.opExtrude","SWEPT_EDGE",EDGE,{"disambiguationData":[OSD([sQuery(id+"F0.wireOp",EDGE,"E22.0"),sQuery(id+"F0.wireOp",EDGE,"E32")])]});
            var Q51;
            {var subQ0=sQuery(id+"F0.wireOp",EDGE,"E32");Q51=makeQuery(id+"F1.opExtrude","CAP_EDGE",EDGE,{"disambiguationData":[OSD([subQ0]),TDD([makeQuery(id+"F0.imprint","IMPRINT",EDGE,{"disambiguationData":[TD([[makeQuery(id+"F0.imprint","INTERSECT",VERTEX,{"derivedFrom":[sQuery(id+"F0.wireOp",EDGE,"E14"),subQ0]}),1.0]])],"derivedFrom":subQ0})])],"isStart":true});}
            var Q52;
            Q52=makeQuery(id+"F1.opExtrude","CAP_EDGE",EDGE,{"disambiguationData":[OSD([sQuery(id+"F0.wireOp",EDGE,"E14")])],"isStart":true});
            var Q53;
            Q53=makeQuery(id+"F1.opExtrude","SWEPT_EDGE",EDGE,{"disambiguationData":[OSD([sQuery(id+"F0.wireOp",EDGE,"E14"),sQuery(id+"F0.wireOp",EDGE,"E32")])]});
            var Q54;
            Q54=makeQuery(id+"F3.opExtrude","SWEPT_EDGE",EDGE,{"disambiguationData":[OSD([sQuery(id+"F0.wireOp",EDGE,"E12.0"),sQuery(id+"F0.wireOp",EDGE,"E34")])]});
            var Q55;
            Q55=makeQuery(id+"F3.opExtrude","SWEPT_EDGE",EDGE,{"disambiguationData":[OSD([sQuery(id+"F0.wireOp",EDGE,"E12.0"),sQuery(id+"F0.wireOp",EDGE,"E35")])]});
            var Q56;
            Q56=makeQuery(id+"F3.opExtrude","CAP_EDGE",EDGE,{"disambiguationData":[OSD([sQuery(id+"F0.wireOp",EDGE,"E12.0")])],"isStart":false});
            var Q57;
            Q57=makeQuery(id+"F3.opExtrude","CAP_EDGE",EDGE,{"disambiguationData":[OSD([sQuery(id+"F0.wireOp",EDGE,"E34")])],"isStart":false});
            var Q58;
            Q58=makeQuery(id+"F3.opExtrude","CAP_EDGE",EDGE,{"disambiguationData":[OSD([sQuery(id+"F0.wireOp",EDGE,"E35")])],"isStart":false});
            var Q59;
            {var subQ0=sQuery(id+"F0.wireOp",EDGE,"E17");var subQ1=sQuery(id+"F0.wireOp",EDGE,"E12.0");Q59=makeQuery(id+"F3.boolean.opBoolean","SPLIT",EDGE,{"disambiguationData":[TD([makeQuery(id+"F1.opExtrude","SWEPT_FACE",FACE,{"disambiguationData":[OSD([subQ0])]})])],"derivedFrom":makeQuery(id+"F1.opExtrude","CAP_EDGE",EDGE,{"disambiguationData":[OSD([subQ1])],"isStart":true})});}
            var Q60;
            Q60=makeQuery(id+"F1.opExtrude","CAP_EDGE",EDGE,{"disambiguationData":[OSD([sQuery(id+"F0.wireOp",EDGE,"E11.0")])],"isStart":true});
            var Q61;
            {var subQ0=sQuery(id+"F0.wireOp",EDGE,"E32");Q61=makeQuery(id+"F1.opExtrude","CAP_EDGE",EDGE,{"disambiguationData":[OSD([subQ0]),TDD([makeQuery(id+"F0.imprint","IMPRINT",EDGE,{"disambiguationData":[TD([[makeQuery(id+"F0.imprint","INTERSECT",VERTEX,{"derivedFrom":[sQuery(id+"F0.wireOp",EDGE,"E15"),subQ0]}),-1.0]])],"derivedFrom":subQ0})])],"isStart":true});}
            var Q62;
            Q62=makeQuery(id+"F1.opExtrude","SWEPT_EDGE",EDGE,{"disambiguationData":[OSD([sQuery(id+"F0.wireOp",EDGE,"E15"),sQuery(id+"F0.wireOp",EDGE,"E32")])]});
            var Q63;
            Q63=makeQuery(id+"F1.opExtrude","CAP_EDGE",EDGE,{"disambiguationData":[OSD([sQuery(id+"F0.wireOp",EDGE,"E26.0")])],"isStart":true});
            var Q64;
            Q64=makeQuery(id+"F1.opExtrude","SWEPT_EDGE",EDGE,{"disambiguationData":[OSD([sQuery(id+"F0.wireOp",EDGE,"E27.0"),sQuery(id+"F0.wireOp",EDGE,"E32")])]});
            var Q65;
            Q65=makeQuery(id+"F1.opExtrude","SWEPT_EDGE",EDGE,{"disambiguationData":[OSD([sQuery(id+"F0.wireOp",EDGE,"E26.0"),sQuery(id+"F0.wireOp",EDGE,"E32")])]});
            var Q66;
            Q66=makeQuery(id+"F3.opExtrude","SWEPT_EDGE",EDGE,{"disambiguationData":[OSD([sQuery(id+"F0.wireOp",EDGE,"E35"),sQuery(id+"F0.wireOp",EDGE,"E36")])]});
            var Q67;
            Q67=makeQuery(id+"F3.opExtrude","CAP_EDGE",EDGE,{"disambiguationData":[OSD([sQuery(id+"F0.wireOp",EDGE,"E36")])],"isStart":false});
            var Q68;
            Q68=makeQuery(id+"F3.opExtrude","SWEPT_EDGE",EDGE,{"disambiguationData":[OSD([sQuery(id+"F0.wireOp",EDGE,"E34"),sQuery(id+"F0.wireOp",EDGE,"E36")])]});
            var Q69;
            {var subQ0=sQuery(id+"F0.wireOp",EDGE,"E32");var subQ1=makeQuery(id+"F0.imprint","INTERSECT",VERTEX,{"derivedFrom":[sQuery(id+"F0.wireOp",EDGE,"E0.35"),subQ0]});Q69=makeQuery(id+"F1.opExtrude","CAP_EDGE",EDGE,{"disambiguationData":[OSD([subQ0]),TDD([makeQuery(id+"F0.imprint","IMPRINT",EDGE,{"disambiguationData":[TD([[subQ1,1.0]])],"derivedFrom":subQ0}),makeQuery(id+"F0.imprint","IMPRINT",EDGE,{"disambiguationData":[TD([[makeQuery(id+"F0.imprint","INTERSECT",VERTEX,{"derivedFrom":[sQuery(id+"F0.wireOp",EDGE,"E0.32"),subQ0]}),1.0]])],"derivedFrom":subQ0})])],"isStart":true});}
            var Q70;
            Q70=makeQuery(id+"F2.opExtrude","CAP_EDGE",EDGE,{"disambiguationData":[OSD([sQuery(id+"F0.wireOp",EDGE,"E0.34")])],"isStart":false});
            var Q71;
            Q71=makeQuery(id+"F2.opExtrude","CAP_EDGE",EDGE,{"disambiguationData":[OSD([sQuery(id+"F0.wireOp",EDGE,"E0.35")])],"isStart":false});
            var Q72;
            Q72=makeQuery(id+"F2.opExtrude","CAP_EDGE",EDGE,{"disambiguationData":[OSD([sQuery(id+"F0.wireOp",EDGE,"E32")])],"isStart":false});
            var Q73;
            Q73=makeQuery(id+"F2.opExtrude","CAP_EDGE",EDGE,{"disambiguationData":[OSD([sQuery(id+"F0.wireOp",EDGE,"E0.32")])],"isStart":false});
            var Q74;
            Q74=makeQuery(id+"F2.opExtrude","CAP_EDGE",EDGE,{"disambiguationData":[OSD([sQuery(id+"F0.wireOp",EDGE,"E0.33")])],"isStart":false});
            var Q75;
            Q75=makeQuery(id+"F2.opExtrude","SWEPT_EDGE",EDGE,{"disambiguationData":[OSD([sQuery(id+"F0.wireOp",EDGE,"E0.32"),sQuery(id+"F0.wireOp",EDGE,"E0.33"),sQuery(id+"F0.wireOp",EDGE,"E37"),sQuery(id+"F0.wireOp",EDGE,"E40")])]});
            var Q76;
            Q76=makeQuery(id+"F2.opExtrude","SWEPT_EDGE",EDGE,{"disambiguationData":[OSD([sQuery(id+"F0.wireOp",EDGE,"E0.33"),sQuery(id+"F0.wireOp",EDGE,"E0.34")])]});
            var Q77;
            Q77=makeQuery(id+"F1.opExtrude","CAP_EDGE",EDGE,{"disambiguationData":[OSD([sQuery(id+"F0.wireOp",EDGE,"E0.31"),sQuery(id+"F0.wireOp",EDGE,"E0.32"),sQuery(id+"F0.wireOp",EDGE,"E40")])],"isStart":true});
            var Q78;
            Q78=makeQuery(id+"F2.opExtrude","SWEPT_EDGE",EDGE,{"disambiguationData":[OSD([sQuery(id+"F0.wireOp",EDGE,"E0.29"),sQuery(id+"F0.wireOp",EDGE,"E0.31"),sQuery(id+"F0.wireOp",EDGE,"E39"),sQuery(id+"F0.wireOp",EDGE,"E40")])]});
            var Q79;
            Q79=makeQuery(id+"F2.opExtrude","CAP_EDGE",EDGE,{"disambiguationData":[OSD([sQuery(id+"F0.wireOp",EDGE,"E0.31")])],"isStart":false});
            var Q80;
            Q80=makeQuery(id+"F2.opExtrude","CAP_EDGE",EDGE,{"disambiguationData":[OSD([sQuery(id+"F0.wireOp",EDGE,"E0.28")])],"isStart":false});
            var Q81;
            Q81=makeQuery(id+"F2.opExtrude","CAP_EDGE",EDGE,{"disambiguationData":[OSD([sQuery(id+"F0.wireOp",EDGE,"E0.29")])],"isStart":false});
            var Q82;
            Q82=makeQuery(id+"F2.opExtrude","CAP_EDGE",EDGE,{"disambiguationData":[OSD([sQuery(id+"F0.wireOp",EDGE,"E0.30")])],"isStart":false});
            var Q83;
            Q83=makeQuery(id+"F2.opExtrude","CAP_EDGE",EDGE,{"disambiguationData":[OSD([sQuery(id+"F0.wireOp",EDGE,"E0.17")])],"isStart":false});
            var Q84;
            Q84=makeQuery(id+"F2.opExtrude","CAP_EDGE",EDGE,{"disambiguationData":[OSD([sQuery(id+"F0.wireOp",EDGE,"E0.15")])],"isStart":false});
            var Q85;
            Q85=makeQuery(id+"F2.opExtrude","SWEPT_EDGE",EDGE,{"disambiguationData":[OSD([sQuery(id+"F0.wireOp",EDGE,"E0.28"),sQuery(id+"F0.wireOp",EDGE,"E0.29")])]});
            var Q86;
            Q86=makeQuery(id+"F2.opExtrude","CAP_EDGE",EDGE,{"disambiguationData":[OSD([sQuery(id+"F0.wireOp",EDGE,"E0.14")])],"isStart":false});
            var Q87;
            {var subQ0=sQuery(id+"F0.wireOp",EDGE,"E46");var subQ1=makeQuery(id+"F0.imprint","INTERSECT",VERTEX,{"derivedFrom":[sQuery(id+"F0.wireOp",EDGE,"E0.26"),sQuery(id+"F0.wireOp",EDGE,"E33"),subQ0]});var subQ2=makeQuery(id+"F0.imprint","INTERSECT",VERTEX,{"derivedFrom":[sQuery(id+"F0.wireOp",EDGE,"E0.24"),subQ0]});var subQ4=makeQuery(id+"F0.imprint","INTERSECT",VERTEX,{"derivedFrom":[sQuery(id+"F0.wireOp",EDGE,"E0.8"),subQ0]});var subQ5=makeQuery(id+"F0.imprint","INTERSECT",VERTEX,{"derivedFrom":[sQuery(id+"F0.wireOp",EDGE,"E0.6"),subQ0]});Q87=makeQuery(id+"F4.opExtrude","CAP_EDGE",EDGE,{"disambiguationData":[OSD([subQ0]),TDD([makeQuery(id+"F0.imprint","IMPRINT",EDGE,{"disambiguationData":[TD([[subQ5,1.0]])],"derivedFrom":subQ0}),makeQuery(id+"F0.imprint","IMPRINT",EDGE,{"disambiguationData":[TD([[subQ5,-1.0]])],"derivedFrom":subQ0}),makeQuery(id+"F0.imprint","IMPRINT",EDGE,{"disambiguationData":[TD([[subQ4,-1.0]])],"derivedFrom":subQ0}),makeQuery(id+"F0.imprint","IMPRINT",EDGE,{"disambiguationData":[TD([[subQ2,1.0]])],"derivedFrom":subQ0}),makeQuery(id+"F0.imprint","IMPRINT",EDGE,{"disambiguationData":[TD([[subQ2,-1.0]])],"derivedFrom":subQ0}),makeQuery(id+"F0.imprint","IMPRINT",EDGE,{"disambiguationData":[TD([[subQ1,-1.0]])],"derivedFrom":subQ0})])],"isStart":false});}
            var Q88;
            Q88=makeQuery(id+"F4.opExtrude","CAP_EDGE",EDGE,{"disambiguationData":[OSD([sQuery(id+"F0.wireOp",EDGE,"E48")])],"isStart":false});
            fillet(context, id + "F7", {"entities" : qUnion([Q0, Q1, Q2, Q3, Q4, Q5, Q6, Q7, Q8, Q9, Q10, Q11, Q12, Q13, Q14, Q15, Q16, Q17, Q18, Q19, Q20, Q21, Q22, Q23, Q24, Q25, Q26, Q27, Q28, Q29, Q30, Q31, Q32, Q33, Q34, Q35, Q36, Q37, Q38, Q39, Q40, Q41, Q42, Q43, Q44, Q45, Q46, Q47, Q48, Q49, Q50, Q51, Q52, Q53, Q54, Q55, Q56, Q57, Q58, Q59, Q60, Q61, Q62, Q63, Q64, Q65, Q66, Q67, Q68, Q69, Q70, Q71, Q72, Q73, Q74, Q75, Q76, Q77, Q78, Q79, Q80, Q81, Q82, Q83, Q84, Q85, Q86, Q87, Q88]), "radius" : .15 * mm, "tangentPropagation" : true, "allowEdgeOverflow" : false});
        }
        {
            var Q0;
            {var subQ0=sQuery(id+"F0.wireOp",EDGE,"E45");var subQ1=sQuery(id+"F0.wireOp",EDGE,"E31");var subQ2=sQuery(id+"F0.wireOp",EDGE,"E20");var subQ3=sQuery(id+"F0.wireOp",EDGE,"E0.14");Q0=makeQuery(id+"F5.boolean.opBoolean","MERGE",EDGE,{"derivedFrom":[makeQuery(id+"F2.opExtrude","SWEPT_EDGE",EDGE,{"disambiguationData":[OSD([subQ3,subQ2,subQ1,subQ0])]}),makeQuery(id+"F5.opExtrude","SWEPT_EDGE",EDGE,{"disambiguationData":[OSD([subQ3,subQ2,subQ1,subQ0])]})]});}
            var Q1;
            Q1=makeQuery(id+"F4.boolean.opBoolean","SPLIT",EDGE,{"derivedFrom":makeQuery(id+"F2.opExtrude","SWEPT_EDGE",EDGE,{"disambiguationData":[OSD([sQuery(id+"F0.wireOp",EDGE,"E0.20"),sQuery(id+"F0.wireOp",EDGE,"E0.21"),sQuery(id+"F0.wireOp",EDGE,"E46"),sQuery(id+"F0.wireOp",EDGE,"E48")])]})});
            var Q2;
            {var subQ0=sQuery(id+"F0.wireOp",EDGE,"E45");var subQ1=sQuery(id+"F0.wireOp",EDGE,"E33");var subQ2=sQuery(id+"F0.wireOp",EDGE,"E20");var subQ3=sQuery(id+"F0.wireOp",EDGE,"E0.20");Q2=makeQuery(id+"F5.boolean.opBoolean","MERGE",EDGE,{"derivedFrom":[makeQuery(id+"F2.opExtrude","SWEPT_EDGE",EDGE,{"disambiguationData":[OSD([subQ3,subQ2,subQ1,subQ0])]}),makeQuery(id+"F5.opExtrude","SWEPT_EDGE",EDGE,{"disambiguationData":[OSD([subQ3,subQ2,subQ1,subQ0])]})]});}
            var Q3;
            {var subQ0=sQuery(id+"F0.wireOp",EDGE,"E32");var subQ1=sQuery(id+"F0.wireOp",EDGE,"E0.32");Q3=makeQuery(id+"F2.boolean.opBoolean","MERGE",EDGE,{"derivedFrom":[makeQuery(id+"F1.opExtrude","SWEPT_EDGE",EDGE,{"disambiguationData":[OSD([subQ1,subQ0])]}),makeQuery(id+"F2.opExtrude","SWEPT_EDGE",EDGE,{"disambiguationData":[OSD([subQ1,subQ0])]})]});}
            var Q4;
            Q4=makeQuery(id+"F2.opExtrude","SWEPT_EDGE",EDGE,{"disambiguationData":[OSD([sQuery(id+"F0.wireOp",EDGE,"E0.35"),sQuery(id+"F0.wireOp",EDGE,"E32")])]});
            var Q5;
            Q5=makeQuery(id+"F2.opExtrude","SWEPT_EDGE",EDGE,{"disambiguationData":[OSD([sQuery(id+"F0.wireOp",EDGE,"E0.34"),sQuery(id+"F0.wireOp",EDGE,"E0.35")])]});
            fillet(context, id + "F8", {"entities" : qUnion([Q0, Q1, Q2, Q3, Q4, Q5]), "radius" : .15 * mm, "allowEdgeOverflow" : false});
        }
    });
